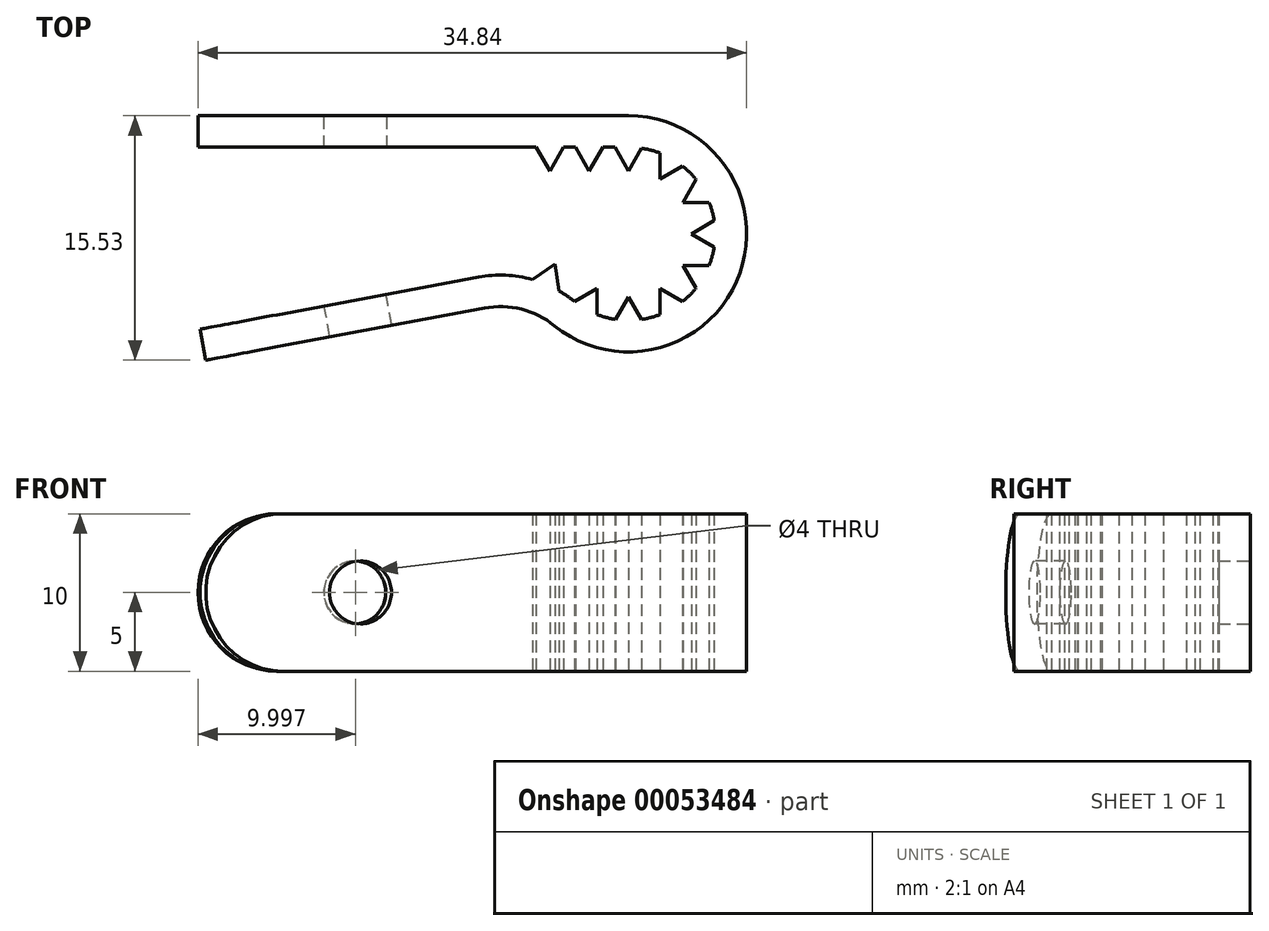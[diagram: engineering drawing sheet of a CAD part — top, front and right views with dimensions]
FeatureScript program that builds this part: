
annotation { "Feature Type Name" : "Feature", "Feature Type Description" : "" }
export const myFeature = defineFeature(function(context is Context, id is Id, definition is map)
    precondition{}
    {
        {
            var Q0;
            Q0=qCreatedBy(makeId("Top.planeOp"),FACE);
            var sketch = newSketch(context, id + "F0", { "sketchPlane" : qUnion([Q0])});
            skArc(sketch, "E0", {"start": v(2, 5.12) * mm, "mid": v(-0.83, 5.44) * mm, "end": v(-3.44, 4.3) * mm});
            skLineSegment(sketch, "E1", {"start": v(5.5, 0.06) * mm, "end": v(-27.22, -6.06) * mm, "construction": true});
            skLineSegment(sketch, "E2", {"start": v(5.5, 0.06) * mm, "end": v(-7.5, 0.06) * mm, "construction": true});
            skLineSegment(sketch, "E3", {"start": v(0, 7.5) * mm, "end": v(-27.34, 7.5) * mm});
            skLineSegment(sketch, "E4.0", {"start": v(0, 5.5) * mm, "end": v(-27.34, 5.5) * mm});
            skLineSegment(sketch, "E5", {"start": v(-27.34, 7.5) * mm, "end": v(-27.34, 5.5) * mm});
            skArc(sketch, "E6", {"start": v(-3.45, -4.28) * mm, "mid": v(-6.32, -2.85) * mm, "end": v(-9.53, -2.75) * mm});
            skArc(sketch, "E7", {"start": v(-27.34, 5.5) * mm, "mid": v(-27.89, -0.29) * mm, "end": v(-27.22, -6.06) * mm, "construction": true});
            skLineSegment(sketch, "E8", {"start": v(5.5, 0.06) * mm, "end": v(-27.34, 5.5) * mm, "construction": true});
            skLineSegment(sketch, "E9", {"start": v(-9.53, -2.75) * mm, "end": v(-27.22, -6.06) * mm});
            skLineSegment(sketch, "E10.0", {"start": v(-9.16, -4.72) * mm, "end": v(-26.86, -8.03) * mm});
            skLineSegment(sketch, "E11", {"start": v(-27.22, -6.06) * mm, "end": v(-26.86, -8.03) * mm});
            skLineSegment(sketch, "E12", {"start": v(-9.16, -4.72) * mm, "end": v(-9.53, -2.75) * mm});
            skArc(sketch, "E13", {"start": v(-4.7, -5.84) * mm, "mid": v(-6.81, -4.8) * mm, "end": v(-9.16, -4.72) * mm});
            skCircle(sketch, "E14", {"center": v(0, 0) * mm, "radius": 4 * mm, "construction": true});
            skLineSegment(sketch, "E15", {"start": v(0, 4) * mm, "end": v(0.87, 5.5) * mm});
            skLineSegment(sketch, "E16", {"start": v(0.87, 5.5) * mm, "end": v(-0.87, 5.5) * mm});
            skLineSegment(sketch, "E17", {"start": v(-0.87, 5.5) * mm, "end": v(0, 4) * mm});
            skLineSegment(sketch, "E18.1.0", {"start": v(-2, 3.46) * mm, "end": v(-2, 5.2) * mm});
            skLineSegment(sketch, "E18.1.1", {"start": v(-3.5, 4.33) * mm, "end": v(-3.44, 4.3) * mm});
            skLineSegment(sketch, "E18.5.0", {"start": v(-2, -3.46) * mm, "end": v(-3.5, -4.33) * mm});
            skLineSegment(sketch, "E18.5.1", {"start": v(-2, -5.2) * mm, "end": v(-2, -3.46) * mm});
            skLineSegment(sketch, "E18.6.0", {"start": v(0, -4) * mm, "end": v(-0.87, -5.5) * mm});
            skLineSegment(sketch, "E18.6.1", {"start": v(0.87, -5.5) * mm, "end": v(0, -4) * mm});
            skLineSegment(sketch, "E18.7.0", {"start": v(2, -3.46) * mm, "end": v(2, -5.2) * mm});
            skLineSegment(sketch, "E18.7.1", {"start": v(3.5, -4.33) * mm, "end": v(2, -3.46) * mm});
            skLineSegment(sketch, "E18.8.0", {"start": v(3.46, -2) * mm, "end": v(4.33, -3.5) * mm});
            skLineSegment(sketch, "E18.8.1", {"start": v(5.2, -2) * mm, "end": v(3.46, -2) * mm});
            skLineSegment(sketch, "E18.9.0", {"start": v(4, 0) * mm, "end": v(5.5, -0.87) * mm});
            skLineSegment(sketch, "E18.9.1", {"start": v(5.5, 0.87) * mm, "end": v(4, 0) * mm});
            skLineSegment(sketch, "E18.10.0", {"start": v(3.46, 2) * mm, "end": v(5.2, 2) * mm});
            skLineSegment(sketch, "E18.10.1", {"start": v(4.33, 3.5) * mm, "end": v(3.46, 2) * mm});
            skLineSegment(sketch, "E18.11.0", {"start": v(2, 3.46) * mm, "end": v(3.5, 4.33) * mm});
            skLineSegment(sketch, "E18.11.1", {"start": v(2, 5.2) * mm, "end": v(2, 3.46) * mm});
            skLineSegment(sketch, "E19", {"start": v(-5.23, -3.22) * mm, "end": v(-4.68, -1.92) * mm});
            skLineSegment(sketch, "E20", {"start": v(-4.68, -1.92) * mm, "end": v(-4.4, -3.63) * mm});
            skLineSegment(sketch, "E21", {"start": v(-6.1, -2.91) * mm, "end": v(-4.68, -1.92) * mm});
            skLineSegment(sketch, "E22", {"start": v(0, 4) * mm, "end": v(0, 5.5) * mm});
            skPoint(sketch, "E23.orphan", {"position": v(-4.33, -3.5) * mm});
            skLineSegment(sketch, "E24.1.0.0", {"start": v(-3.37, 5.5) * mm, "end": v(-2.5, 4) * mm});
            skLineSegment(sketch, "E24.1.0.1", {"start": v(-2.5, 4) * mm, "end": v(-1.63, 5.5) * mm});
            skLineSegment(sketch, "E24.2.0.0", {"start": v(-5.87, 5.5) * mm, "end": v(-5, 4) * mm});
            skLineSegment(sketch, "E24.2.0.1", {"start": v(-5, 4) * mm, "end": v(-4.13, 5.5) * mm});
            skLineSegment(sketch, "E24.direction1", {"start": v(0, 4) * mm, "end": v(-2.5, 4) * mm, "construction": true});
            skArc(sketch, "E25.trimOffspring", {"start": v(-7.14, -2.3) * mm, "mid": v(6.06, -4.41) * mm, "end": v(0, 7.5) * mm});
            skArc(sketch, "E26.trimOffspring", {"start": v(4.3, 3.44) * mm, "mid": v(3.89, 3.89) * mm, "end": v(3.44, 4.3) * mm});
            skArc(sketch, "E27.trimOffspring", {"start": v(-5.19, 1.83) * mm, "mid": v(0.1, -5.5) * mm, "end": v(5.12, 2) * mm});
            skSolve(sketch);
        }
        {
            var Q0;
            {var subQ0=sQuery(id+"F0.wireOp",EDGE,"E24.2.0.0");Q0=makeQuery(id+"F0.imprint","IMPRINT",FACE,{"disambiguationData":[TD([[makeQuery(id+"F0.imprint","IMPRINT",EDGE,{"derivedFrom":subQ0}),1.0]])]});}
            var Q1;
            Q1=makeQuery(id+"F0.imprint","IMPRINT",FACE,{"disambiguationData":[TD([[makeQuery(id+"F0.imprint","IMPRINT",EDGE,{"derivedFrom":sQuery(id+"F0.wireOp",EDGE,"E9")}),1.0]])]});
            var Q2;
            {var subQ0=sQuery(id+"F0.wireOp",EDGE,"E18.5.1");var subQ1=sQuery(id+"F0.wireOp",EDGE,"E18.5.0");var subQ2=makeQuery(id+"F0.imprint","INTERSECT",VERTEX,{"derivedFrom":[subQ1,subQ0]});Q2=makeQuery(id+"F0.imprint","IMPRINT",FACE,{"disambiguationData":[TD([[makeQuery(id+"F0.imprint","IMPRINT",EDGE,{"disambiguationData":[TD([[subQ2,-1.0]])],"derivedFrom":subQ1}),1.0]])]});}
            var Q3;
            {var subQ0=sQuery(id+"F0.wireOp",EDGE,"E18.6.1");var subQ1=sQuery(id+"F0.wireOp",EDGE,"E18.6.0");var subQ2=makeQuery(id+"F0.imprint","INTERSECT",VERTEX,{"derivedFrom":[subQ1,subQ0]});Q3=makeQuery(id+"F0.imprint","IMPRINT",FACE,{"disambiguationData":[TD([[makeQuery(id+"F0.imprint","IMPRINT",EDGE,{"disambiguationData":[TD([[subQ2,-1.0]])],"derivedFrom":subQ1}),1.0]])]});}
            var Q4;
            {var subQ0=sQuery(id+"F0.wireOp",EDGE,"E18.7.1");var subQ1=sQuery(id+"F0.wireOp",EDGE,"E18.7.0");var subQ2=makeQuery(id+"F0.imprint","INTERSECT",VERTEX,{"derivedFrom":[subQ1,subQ0]});Q4=makeQuery(id+"F0.imprint","IMPRINT",FACE,{"disambiguationData":[TD([[makeQuery(id+"F0.imprint","IMPRINT",EDGE,{"disambiguationData":[TD([[subQ2,-1.0]])],"derivedFrom":subQ1}),1.0]])]});}
            var Q5;
            {var subQ0=sQuery(id+"F0.wireOp",EDGE,"E18.8.1");var subQ1=sQuery(id+"F0.wireOp",EDGE,"E18.8.0");var subQ2=makeQuery(id+"F0.imprint","INTERSECT",VERTEX,{"derivedFrom":[subQ1,subQ0]});Q5=makeQuery(id+"F0.imprint","IMPRINT",FACE,{"disambiguationData":[TD([[makeQuery(id+"F0.imprint","IMPRINT",EDGE,{"disambiguationData":[TD([[subQ2,-1.0]])],"derivedFrom":subQ1}),1.0]])]});}
            var Q6;
            {var subQ0=sQuery(id+"F0.wireOp",EDGE,"E18.9.1");var subQ1=sQuery(id+"F0.wireOp",EDGE,"E18.9.0");var subQ2=makeQuery(id+"F0.imprint","INTERSECT",VERTEX,{"derivedFrom":[subQ1,subQ0]});Q6=makeQuery(id+"F0.imprint","IMPRINT",FACE,{"disambiguationData":[TD([[makeQuery(id+"F0.imprint","IMPRINT",EDGE,{"disambiguationData":[TD([[subQ2,-1.0]])],"derivedFrom":subQ1}),1.0]])]});}
            var Q7;
            {var subQ0=sQuery(id+"F0.wireOp",EDGE,"E22");Q7=makeQuery(id+"F0.imprint","IMPRINT",FACE,{"disambiguationData":[TD([[makeQuery(id+"F0.imprint","IMPRINT",EDGE,{"derivedFrom":subQ0}),-1.0]])]});}
            var Q8;
            {var subQ0=sQuery(id+"F0.wireOp",EDGE,"E16");var subQ3=sQuery(id+"F0.wireOp",EDGE,"E15");var subQ5=makeQuery(id+"F0.imprint","INTERSECT",VERTEX,{"derivedFrom":[subQ3,subQ0]});Q8=makeQuery(id+"F0.imprint","IMPRINT",FACE,{"disambiguationData":[TD([[makeQuery(id+"F0.imprint","IMPRINT",EDGE,{"disambiguationData":[TD([[subQ5,1.0]])],"derivedFrom":subQ3}),1.0]])]});}
            var Q9;
            {var subQ0=sQuery(id+"F0.wireOp",EDGE,"E22");Q9=makeQuery(id+"F0.imprint","IMPRINT",FACE,{"disambiguationData":[TD([[makeQuery(id+"F0.imprint","IMPRINT",EDGE,{"derivedFrom":subQ0}),1.0]])]});}
            var Q10;
            {var subQ0=sQuery(id+"F0.wireOp",EDGE,"E24.1.0.1");var subQ1=sQuery(id+"F0.wireOp",EDGE,"E0");var subQ2=makeQuery(id+"F0.imprint","INTERSECT",VERTEX,{"derivedFrom":[subQ1,subQ0]});Q10=makeQuery(id+"F0.imprint","IMPRINT",FACE,{"disambiguationData":[TD([[makeQuery(id+"F0.imprint","IMPRINT",EDGE,{"disambiguationData":[TD([[subQ2,-1.0]])],"derivedFrom":subQ1}),1.0]])]});}
            var Q11;
            {var subQ0=sQuery(id+"F0.wireOp",EDGE,"E24.1.0.0");var subQ1=sQuery(id+"F0.wireOp",EDGE,"E0");var subQ2=makeQuery(id+"F0.imprint","INTERSECT",VERTEX,{"derivedFrom":[subQ1,subQ0]});Q11=makeQuery(id+"F0.imprint","IMPRINT",FACE,{"disambiguationData":[TD([[makeQuery(id+"F0.imprint","IMPRINT",EDGE,{"disambiguationData":[TD([[subQ2,1.0]])],"derivedFrom":subQ1}),1.0]])]});}
            var Q12;
            {var subQ0=sQuery(id+"F0.wireOp",EDGE,"E12");Q12=makeQuery(id+"F0.imprint","IMPRINT",FACE,{"disambiguationData":[TD([[makeQuery(id+"F0.imprint","IMPRINT",EDGE,{"derivedFrom":subQ0}),-1.0]])]});}
            var Q13;
            {var subQ0=sQuery(id+"F0.wireOp",EDGE,"E20");var subQ3=sQuery(id+"F0.wireOp",EDGE,"E27.trimOffspring");var subQ5=makeQuery(id+"F0.imprint","INTERSECT",VERTEX,{"derivedFrom":[subQ0,subQ3]});Q13=makeQuery(id+"F0.imprint","IMPRINT",FACE,{"disambiguationData":[TD([[makeQuery(id+"F0.imprint","IMPRINT",EDGE,{"disambiguationData":[TD([[subQ5,1.0]])],"derivedFrom":subQ3}),1.0]])]});}
            var Q14;
            {var subQ0=sQuery(id+"F0.wireOp",EDGE,"E21");var subQ3=sQuery(id+"F0.wireOp",EDGE,"E27.trimOffspring");var subQ5=makeQuery(id+"F0.imprint","INTERSECT",VERTEX,{"derivedFrom":[subQ0,subQ3]});Q14=makeQuery(id+"F0.imprint","IMPRINT",FACE,{"disambiguationData":[TD([[makeQuery(id+"F0.imprint","IMPRINT",EDGE,{"disambiguationData":[TD([[subQ5,-1.0]])],"derivedFrom":subQ3}),1.0]])]});}
            var Q15;
            {var subQ1=sQuery(id+"F0.wireOp",EDGE,"E0");var subQ3=sQuery(id+"F0.wireOp",EDGE,"E17");var subQ4=makeQuery(id+"F0.imprint","INTERSECT",VERTEX,{"derivedFrom":[subQ1,subQ3]});Q15=makeQuery(id+"F0.imprint","IMPRINT",FACE,{"disambiguationData":[TD([[makeQuery(id+"F0.imprint","IMPRINT",EDGE,{"disambiguationData":[TD([[subQ4,1.0]])],"derivedFrom":subQ1}),-1.0]])]});}
            var Q16;
            {var subQ0=sQuery(id+"F0.wireOp",EDGE,"E19");var subQ1=sQuery(id+"F0.wireOp",EDGE,"E6");var subQ2=makeQuery(id+"F0.imprint","INTERSECT",VERTEX,{"derivedFrom":[subQ1,subQ0]});Q16=makeQuery(id+"F0.imprint","IMPRINT",FACE,{"disambiguationData":[TD([[makeQuery(id+"F0.imprint","IMPRINT",EDGE,{"disambiguationData":[TD([[subQ2,-1.0]])],"derivedFrom":subQ1}),-1.0]])]});}
            var Q17;
            {var subQ3=sQuery(id+"F0.wireOp",EDGE,"E0");var subQ5=sQuery(id+"F0.wireOp",EDGE,"E24.1.0.1");var subQ8=makeQuery(id+"F0.imprint","INTERSECT",VERTEX,{"derivedFrom":[subQ3,subQ5]});Q17=makeQuery(id+"F0.imprint","IMPRINT",FACE,{"disambiguationData":[TD([[makeQuery(id+"F0.imprint","IMPRINT",EDGE,{"disambiguationData":[TD([[subQ8,-1.0]])],"derivedFrom":subQ3}),-1.0]])]});}
            var Q18;
            {var subQ0=sQuery(id+"F0.wireOp",EDGE,"E19");var subQ1=sQuery(id+"F0.wireOp",EDGE,"E6");var subQ2=makeQuery(id+"F0.imprint","INTERSECT",VERTEX,{"derivedFrom":[subQ1,subQ0]});Q18=makeQuery(id+"F0.imprint","IMPRINT",FACE,{"disambiguationData":[TD([[makeQuery(id+"F0.imprint","IMPRINT",EDGE,{"disambiguationData":[TD([[subQ2,1.0]])],"derivedFrom":subQ1}),-1.0]])]});}
            var Q19;
            {var subQ14=sQuery(id+"F0.wireOp",EDGE,"E3");Q19=makeQuery(id+"F0.imprint","IMPRINT",FACE,{"disambiguationData":[TD([[makeQuery(id+"F0.imprint","IMPRINT",EDGE,{"derivedFrom":subQ14}),1.0]])]});}
            extrude(context, id + "F1", {"entities" : qUnion([Q0, Q1, Q2, Q3, Q4, Q5, Q6, Q7, Q8, Q9, Q10, Q11, Q12, Q13, Q14, Q15, Q16, Q17, Q18, Q19]), "depth" : 10 * mm});
        }
        {
            var Q0;
            Q0=makeQuery(id+"F1.opExtrude","CAP_EDGE",EDGE,{"disambiguationData":[OSD([sQuery(id+"F0.wireOp",EDGE,"E5")])],"isStart":false});
            var Q1;
            Q1=makeQuery(id+"F1.opExtrude","CAP_EDGE",EDGE,{"disambiguationData":[OSD([sQuery(id+"F0.wireOp",EDGE,"E5")])],"isStart":true});
            var Q2;
            Q2=makeQuery(id+"F1.opExtrude","CAP_EDGE",EDGE,{"disambiguationData":[OSD([sQuery(id+"F0.wireOp",EDGE,"E11")])],"isStart":true});
            var Q3;
            Q3=makeQuery(id+"F1.opExtrude","CAP_EDGE",EDGE,{"disambiguationData":[OSD([sQuery(id+"F0.wireOp",EDGE,"E11")])],"isStart":false});
            fillet(context, id + "F2", {"entities" : qUnion([Q0, Q1, Q2, Q3]), "radius" : 5 * mm, "tangentPropagation" : true, "allowEdgeOverflow" : false});
        }
        {
            var Q0;
            Q0=makeQuery(id+"F1.opExtrude","SWEPT_FACE",FACE,{"disambiguationData":[OSD([sQuery(id+"F0.wireOp",EDGE,"E10.0")])]});
            var sketch = newSketch(context, id + "F3", { "sketchPlane" : qUnion([Q0])});
            skLineSegment(sketch, "E28.0.1", {"start": v(-22.87, 0) * mm, "end": v(-9.87, 0) * mm});
            skArc(sketch, "E29.0", {"start": v(-22.87, 10) * mm, "mid": v(-27.87, 5) * mm, "end": v(-22.87, 0) * mm});
            skLineSegment(sketch, "E30", {"start": v(-27.87, 5) * mm, "end": v(-17.87, 5) * mm, "construction": true});
            skCircle(sketch, "E31", {"center": v(-17.87, 5) * mm, "radius": 2 * mm});
            skSolve(sketch);
        }
        {
            var Q0;
            Q0=makeQuery(id+"F3.imprint","IMPRINT",FACE,{"disambiguationData":[TD([[makeQuery(id+"F3.imprint","IMPRINT",EDGE,{"derivedFrom":sQuery(id+"F3.wireOp",EDGE,"E31")}),1.0]])]});
            extrude(context, id + "F4", {"entities" : qUnion([Q0]), "operationType" : NewBodyOperationType.REMOVE, "oppositeDirection" : true, "depth" : 2 * mm});
        }
        {
            var Q0;
            Q0=makeQuery(id+"F1.opExtrude","SWEPT_FACE",FACE,{"disambiguationData":[OSD([sQuery(id+"F0.wireOp",EDGE,"E3")])]});
            var sketch = newSketch(context, id + "F5", { "sketchPlane" : qUnion([Q0])});
            skArc(sketch, "E32.0", {"start": v(22.34, 0) * mm, "mid": v(27.34, 5) * mm, "end": v(22.34, 10) * mm});
            skLineSegment(sketch, "E33", {"start": v(27.34, 5) * mm, "end": v(17.34, 5) * mm, "construction": true});
            skPoint(sketch, "E33.endSnap0", {"position": v(27.34, 5) * mm});
            skCircle(sketch, "E34", {"center": v(17.34, 5) * mm, "radius": 2 * mm});
            skSolve(sketch);
        }
        {
            var Q0;
            Q0 = qSketchRegion(id + "F5", true);
            extrude(context, id + "F6", {"entities" : qUnion([Q0]), "operationType" : NewBodyOperationType.REMOVE, "oppositeDirection" : true, "depth" : 2 * mm});
        }
    });
